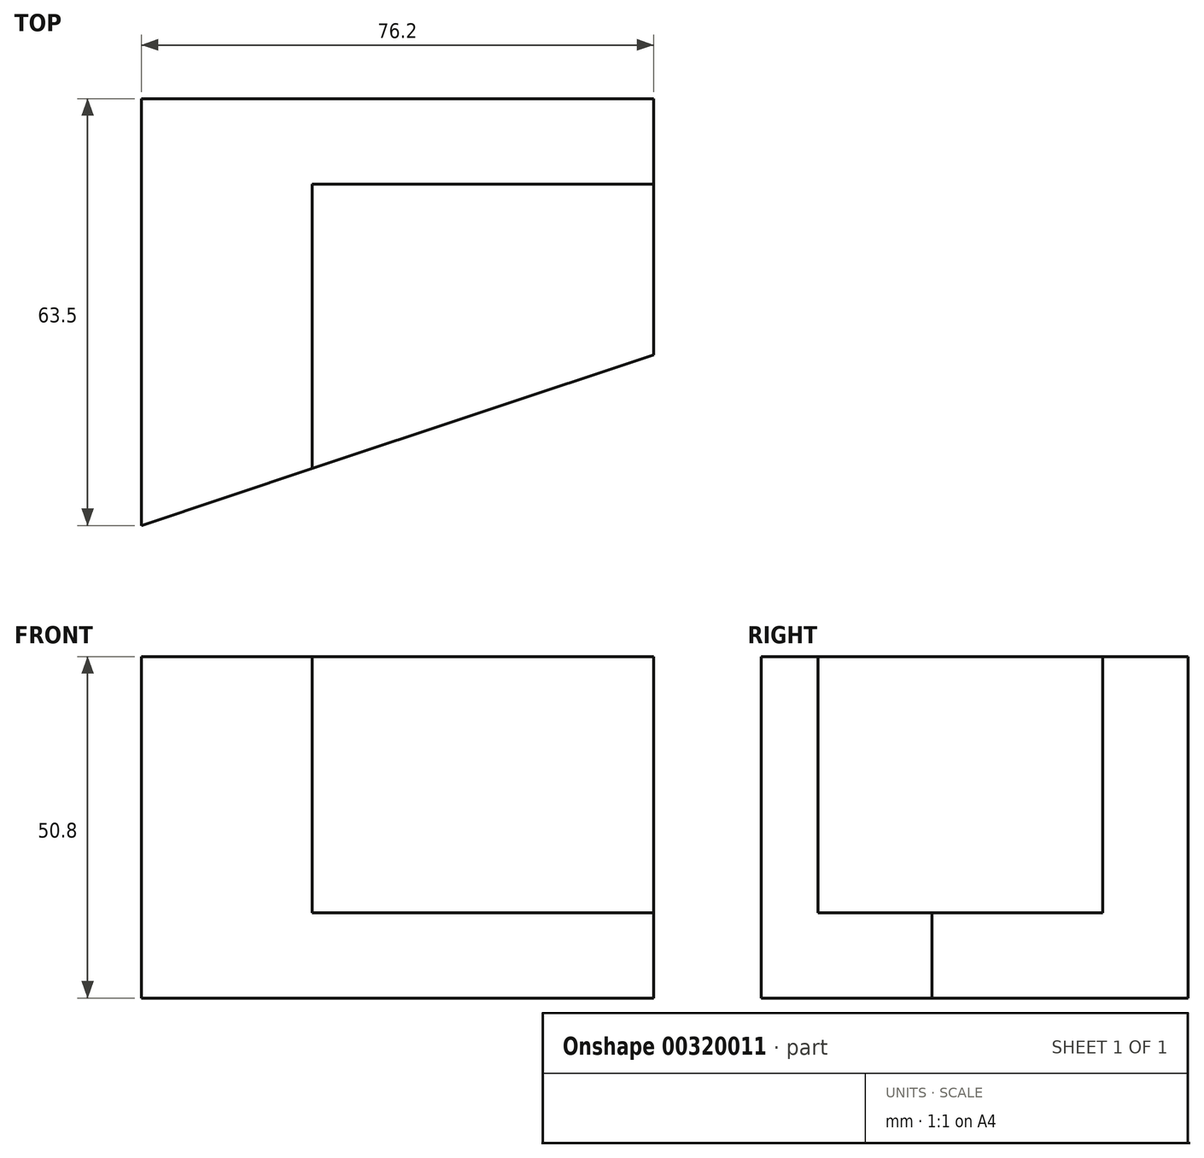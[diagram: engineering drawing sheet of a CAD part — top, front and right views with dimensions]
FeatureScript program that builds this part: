
annotation { "Feature Type Name" : "Feature", "Feature Type Description" : "" }
export const myFeature = defineFeature(function(context is Context, id is Id, definition is map)
    precondition{}
    {
        {
            var Q0;
            Q0=qCreatedBy(makeId("Top.planeOp"),FACE);
            var sketch = newSketch(context, id + "F0", { "sketchPlane" : qUnion([Q0])});
            skLineSegment(sketch, "E0", {"start": v(-23.38, 54.4) * mm, "end": v(52.82, 54.4) * mm});
            skLineSegment(sketch, "E1", {"start": v(52.82, 54.4) * mm, "end": v(52.82, 16.3) * mm});
            skLineSegment(sketch, "E2", {"start": v(-23.38, 54.4) * mm, "end": v(-23.38, -9.1) * mm});
            skLineSegment(sketch, "E3", {"start": v(-23.38, -9.1) * mm, "end": v(52.82, 16.3) * mm});
            skSolve(sketch);
        }
        {
            var Q0;
            Q0 = qSketchRegion(id + "F0", true);
            extrude(context, id + "F1", {"entities" : qUnion([Q0]), "depth" : 50.8 * mm});
        }
        {
            var Q0;
            Q0=makeQuery(id+"F1.opExtrude","CAP_FACE",FACE,{"disambiguationData":[OSD([sQuery(id+"F0.wireOp",EDGE,"E0"),sQuery(id+"F0.wireOp",EDGE,"E1"),sQuery(id+"F0.wireOp",EDGE,"E2"),sQuery(id+"F0.wireOp",EDGE,"E3")])],"isStart":false});
            var sketch = newSketch(context, id + "F2", { "sketchPlane" : qUnion([Q0])});
            skLineSegment(sketch, "E4", {"start": v(52.82, 54.4) * mm, "end": v(52.82, 41.7) * mm});
            skLineSegment(sketch, "E5", {"start": v(52.82, 41.7) * mm, "end": v(2.02, 41.7) * mm});
            skLineSegment(sketch, "E6", {"start": v(2.02, 41.7) * mm, "end": v(2.02, -0.64) * mm});
            skLineSegment(sketch, "E7", {"start": v(2.02, -0.64) * mm, "end": v(52.82, 16.3) * mm});
            skLineSegment(sketch, "E8", {"start": v(52.82, 16.3) * mm, "end": v(52.82, 41.7) * mm});
            skSolve(sketch);
        }
        {
            var Q0;
            Q0 = qSketchRegion(id + "F2", true);
            extrude(context, id + "F3", {"entities" : qUnion([Q0]), "operationType" : NewBodyOperationType.REMOVE, "oppositeDirection" : true, "depth" : 38.1 * mm});
        }
    });
